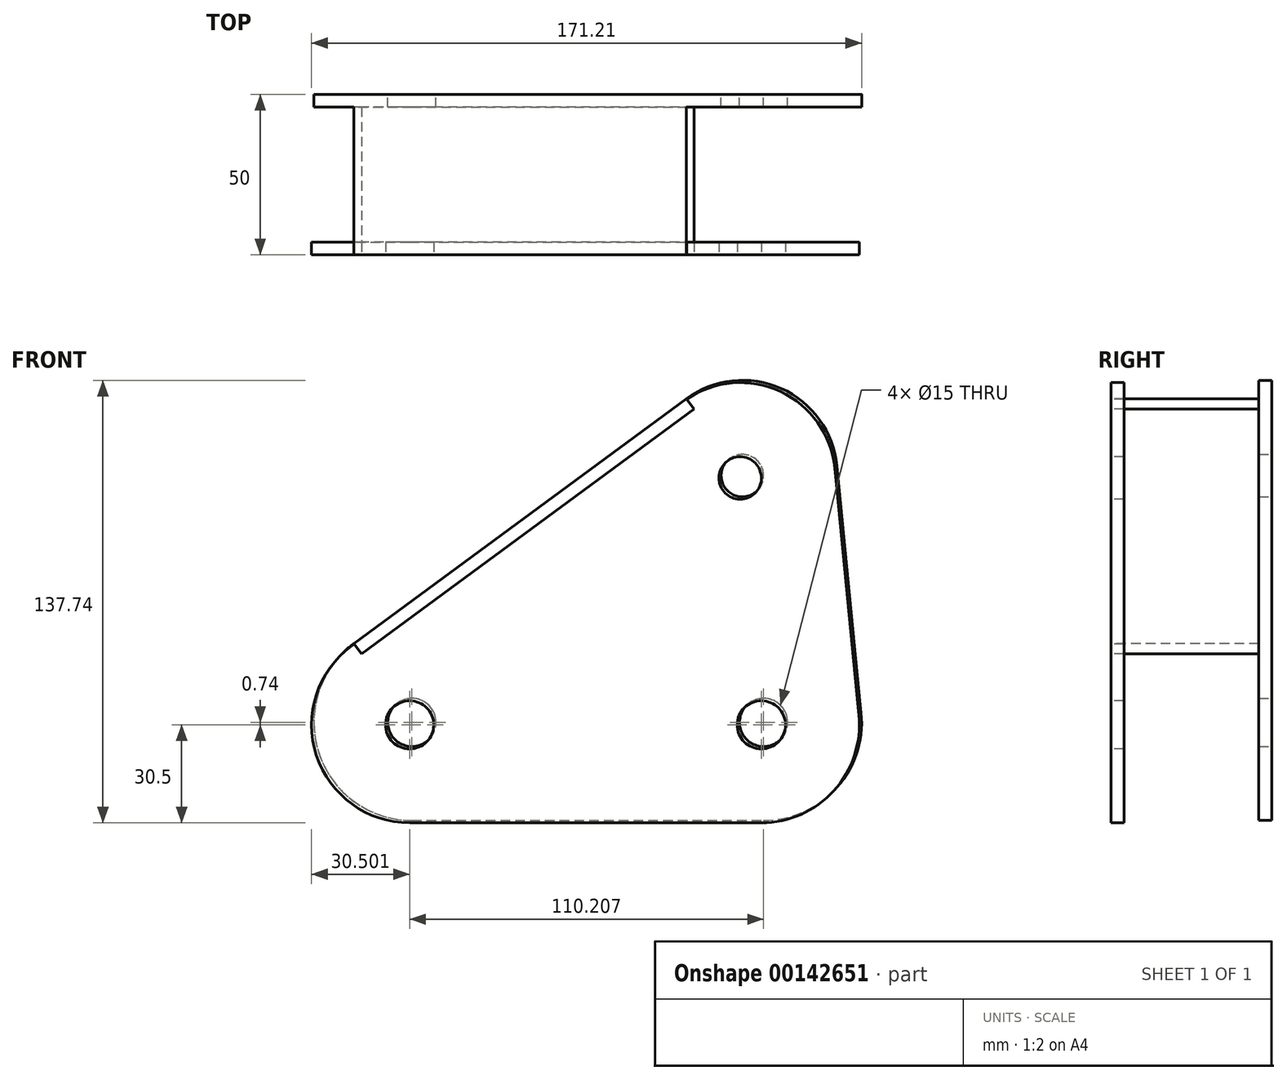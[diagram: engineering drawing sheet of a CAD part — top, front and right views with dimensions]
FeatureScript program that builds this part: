
annotation { "Feature Type Name" : "Feature", "Feature Type Description" : "" }
export const myFeature = defineFeature(function(context is Context, id is Id, definition is map)
    precondition{}
    {
        {
            var Q0;
            Q0=qCreatedBy(makeId("Front.planeOp"),FACE);
            var sketch = newSketch(context, id + "F0", { "sketchPlane" : qUnion([Q0])});
            skCircle(sketch, "E0", {"center": v(29.92, 30.5) * mm, "radius": 7.5 * mm});
            skCircle(sketch, "E1", {"center": v(139.42, 30.5) * mm, "radius": 7.5 * mm});
            skCircle(sketch, "E2", {"center": v(132.8, 107.32) * mm, "radius": 6.6 * mm});
            skPoint(sketch, "E3.visualSharp", {"position": v(113.23, -55.66) * mm});
            skPoint(sketch, "E4.visualSharp", {"position": v(162.42, 161.61) * mm});
            skPoint(sketch, "E5.visualSharp", {"position": v(162.42, -2.22) * mm});
            skLineSegment(sketch, "E6", {"start": v(29.92, 0) * mm, "end": v(139.42, 0) * mm});
            skLineSegment(sketch, "E7", {"start": v(169.77, 33.47) * mm, "end": v(162.25, 110.37) * mm});
            skLineSegment(sketch, "E8", {"start": v(115.4, 131.26) * mm, "end": v(11.84, 55.07) * mm});
            skPoint(sketch, "E9.newPointB", {"position": v(0, 0) * mm});
            skArc(sketch, "E9.filletArc", {"start": v(11.84, 55.07) * mm, "mid": v(0.94, 20.99) * mm, "end": v(29.92, 0) * mm});
            skArc(sketch, "E10.filletArc", {"start": v(162.25, 110.37) * mm, "mid": v(144.9, 134.44) * mm, "end": v(115.4, 131.26) * mm});
            skArc(sketch, "E11.filletArc", {"start": v(139.42, 0) * mm, "mid": v(162, 10.01) * mm, "end": v(169.77, 33.47) * mm});
            skPoint(sketch, "E12.MirrorP", {"position": v(-162.42, 161.61) * mm});
            skSolve(sketch);
        }
        {
            var Q0;
            Q0=makeQuery(id+"F0.imprint","IMPRINT",FACE,{"disambiguationData":[TD([[makeQuery(id+"F0.imprint","IMPRINT",EDGE,{"derivedFrom":sQuery(id+"F0.wireOp",EDGE,"E0")}),-1.0]])]});
            extrude(context, id + "F1", {"entities" : qUnion([Q0]), "depth" : 4 * mm});
        }
        {
            var Q0;
            Q0=makeQuery(id+"F1.opExtrude","SWEPT_FACE",FACE,{"disambiguationData":[OSD([sQuery(id+"F0.wireOp",EDGE,"E8")])]});
            var sketch = newSketch(context, id + "F2", { "sketchPlane" : qUnion([Q0])});
            skLineSegment(sketch, "E13.bottom", {"start": v(170.75, 0) * mm, "end": v(42.17, 0) * mm});
            skLineSegment(sketch, "E13.top", {"start": v(170.75, -50) * mm, "end": v(42.17, -50) * mm});
            skLineSegment(sketch, "E13.left", {"start": v(170.75, 0) * mm, "end": v(170.75, -50) * mm});
            skLineSegment(sketch, "E13.right", {"start": v(42.17, 0) * mm, "end": v(42.17, -50) * mm});
            skSolve(sketch);
        }
        {
            var Q0;
            {var subQ0=sQuery(id+"F2.wireOp",EDGE,"E13.top");Q0=makeQuery(id+"F2.imprint","IMPRINT",FACE,{"disambiguationData":[TD([[makeQuery(id+"F2.imprint","IMPRINT",EDGE,{"derivedFrom":subQ0}),-1.0]])]});}
            extrude(context, id + "F3", {"entities" : qUnion([Q0]), "operationType" : NewBodyOperationType.ADD, "oppositeDirection" : true, "offsetDistance" : 25 * mm, "depth" : 4 * mm});
        }
        {
            var Q0;
            Q0=makeQuery(id+"F3.opExtrude","SWEPT_FACE",FACE,{"disambiguationData":[OSD([sQuery(id+"F2.wireOp",EDGE,"E13.top")])]});
            var sketch = newSketch(context, id + "F4", { "sketchPlane" : qUnion([Q0])});
            skCircle(sketch, "E14", {"center": v(29.21, 29.76) * mm, "radius": 7.5 * mm});
            skCircle(sketch, "E15", {"center": v(138.71, 29.76) * mm, "radius": 7.5 * mm});
            skCircle(sketch, "E16", {"center": v(132.1, 106.58) * mm, "radius": 6.6 * mm});
            skPoint(sketch, "E17.visualSharp", {"position": v(161.71, 160.87) * mm});
            skPoint(sketch, "E18.visualSharp", {"position": v(161.71, -2.96) * mm});
            skLineSegment(sketch, "E19", {"start": v(29.21, -0.74) * mm, "end": v(138.71, -0.74) * mm});
            skLineSegment(sketch, "E20", {"start": v(169.07, 32.73) * mm, "end": v(161.54, 109.63) * mm});
            skLineSegment(sketch, "E21", {"start": v(114.7, 130.52) * mm, "end": v(11.14, 54.33) * mm});
            skPoint(sketch, "E22.newPointB", {"position": v(-0.7, -0.74) * mm});
            skArc(sketch, "E22.filletArc", {"start": v(11.14, 54.33) * mm, "mid": v(0.23, 20.25) * mm, "end": v(29.21, -0.74) * mm});
            skArc(sketch, "E23.filletArc", {"start": v(161.54, 109.63) * mm, "mid": v(144.2, 133.7) * mm, "end": v(114.7, 130.52) * mm});
            skArc(sketch, "E24.filletArc", {"start": v(138.71, -0.74) * mm, "mid": v(161.3, 9.27) * mm, "end": v(169.07, 32.73) * mm});
            skSolve(sketch);
        }
        {
            var Q0;
            Q0=makeQuery(id+"F4.imprint","IMPRINT",FACE,{"disambiguationData":[TD([[makeQuery(id+"F4.imprint","IMPRINT",EDGE,{"derivedFrom":sQuery(id+"F4.wireOp",EDGE,"E14")}),-1.0]])]});
            extrude(context, id + "F5", {"entities" : qUnion([Q0]), "oppositeDirection" : true, "depth" : 4 * mm});
        }
    });
